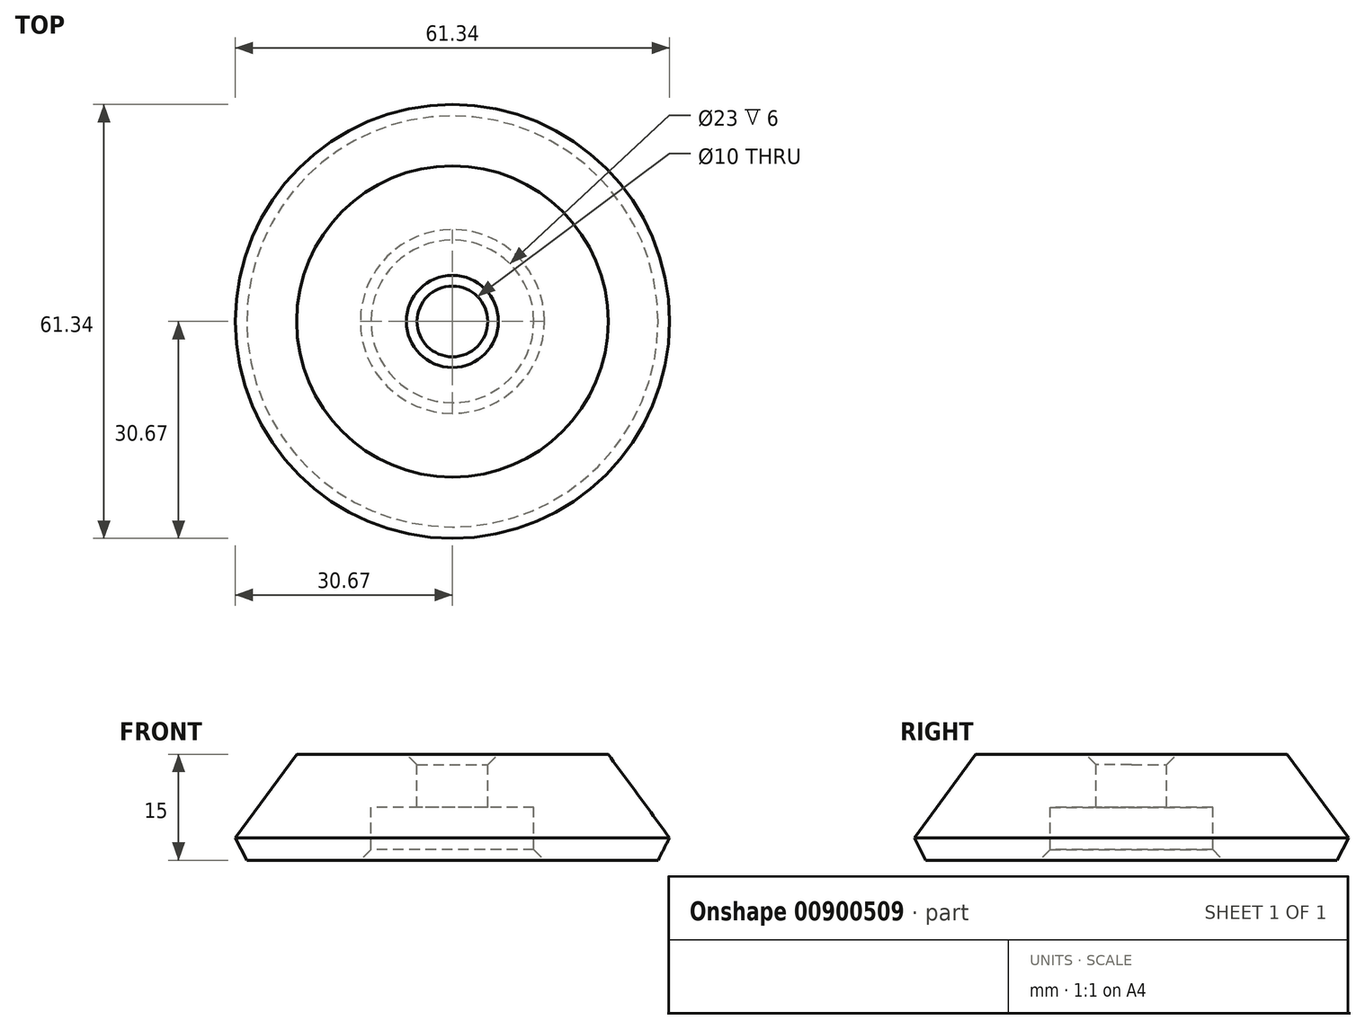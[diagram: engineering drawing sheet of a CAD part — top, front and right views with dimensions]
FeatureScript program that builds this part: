
annotation { "Feature Type Name" : "Feature", "Feature Type Description" : "" }
export const myFeature = defineFeature(function(context is Context, id is Id, definition is map)
    precondition{}
    {
        {
            var Q0;
            Q0=qCreatedBy(makeId("Front.planeOp"),FACE);
            var sketch = newSketch(context, id + "F0", { "sketchPlane" : qUnion([Q0])});
            skLineSegment(sketch, "E0", {"start": v(-11.5, 0) * mm, "end": v(-33, 0) * mm});
            skLineSegment(sketch, "E1", {"start": v(-33, 0) * mm, "end": v(-22, 15) * mm});
            skLineSegment(sketch, "E2", {"start": v(-22, 15) * mm, "end": v(-5, 15) * mm});
            skLineSegment(sketch, "E3", {"start": v(0, 7.5) * mm, "end": v(0, 0) * mm});
            skLineSegment(sketch, "E4", {"start": v(-5, 7.5) * mm, "end": v(-11.5, 7.5) * mm});
            skLineSegment(sketch, "E5", {"start": v(-5, 7.5) * mm, "end": v(-5, 15) * mm});
            skPoint(sketch, "E6.orphan", {"position": v(0, 15) * mm});
            skLineSegment(sketch, "E7", {"start": v(-11.5, 7.5) * mm, "end": v(-5, 7.5) * mm});
            skLineSegment(sketch, "E8", {"start": v(-11.5, 7.5) * mm, "end": v(-11.5, 0) * mm});
            skSolve(sketch);
        }
        {
            var Q0;
            Q0=makeQuery(id+"F0.imprint","IMPRINT",FACE,{"disambiguationData":[TD([[makeQuery(id+"F0.imprint","IMPRINT",EDGE,{"derivedFrom":sQuery(id+"F0.wireOp",EDGE,"E0")}),-1.0]])]});
            var Q1;
            Q1=sQuery(id+"F0.wireOp",EDGE,"E3");
            revolve(context, id + "F1", {"surfaceOperationType" : NewSurfaceOperationType.NEW, "entities" : qUnion([Q0]), "axis" : qUnion([Q1]), "revolveType" : RevolveType.FULL});
        }
        {
            var Q0;
            Q0=makeQuery(id+"F1.opRevolve","SWEPT_EDGE",EDGE,{"disambiguationData":[OSD([sQuery(id+"F0.wireOp",EDGE,"E0"),sQuery(id+"F0.wireOp",EDGE,"E1")])]});
            chamfer(context, id + "F2", {"entities" : qUnion([Q0]), "width" : 2 * mm, "tangentPropagation" : true});
        }
        {
            var Q0;
            Q0=makeQuery(id+"F1.opRevolve","SWEPT_EDGE",EDGE,{"disambiguationData":[OSD([sQuery(id+"F0.wireOp",EDGE,"E2"),sQuery(id+"F0.wireOp",EDGE,"E5")])]});
            chamfer(context, id + "F3", {"entities" : qUnion([Q0]), "width" : 1.5 * mm, "tangentPropagation" : true});
        }
        {
            var Q0;
            Q0=makeQuery(id+"F1.opRevolve","SWEPT_EDGE",EDGE,{"disambiguationData":[OSD([sQuery(id+"F0.wireOp",EDGE,"E0"),sQuery(id+"F0.wireOp",EDGE,"E8")])]});
            chamfer(context, id + "F4", {"entities" : qUnion([Q0]), "width" : 1.5 * mm, "tangentPropagation" : true});
        }
    });
